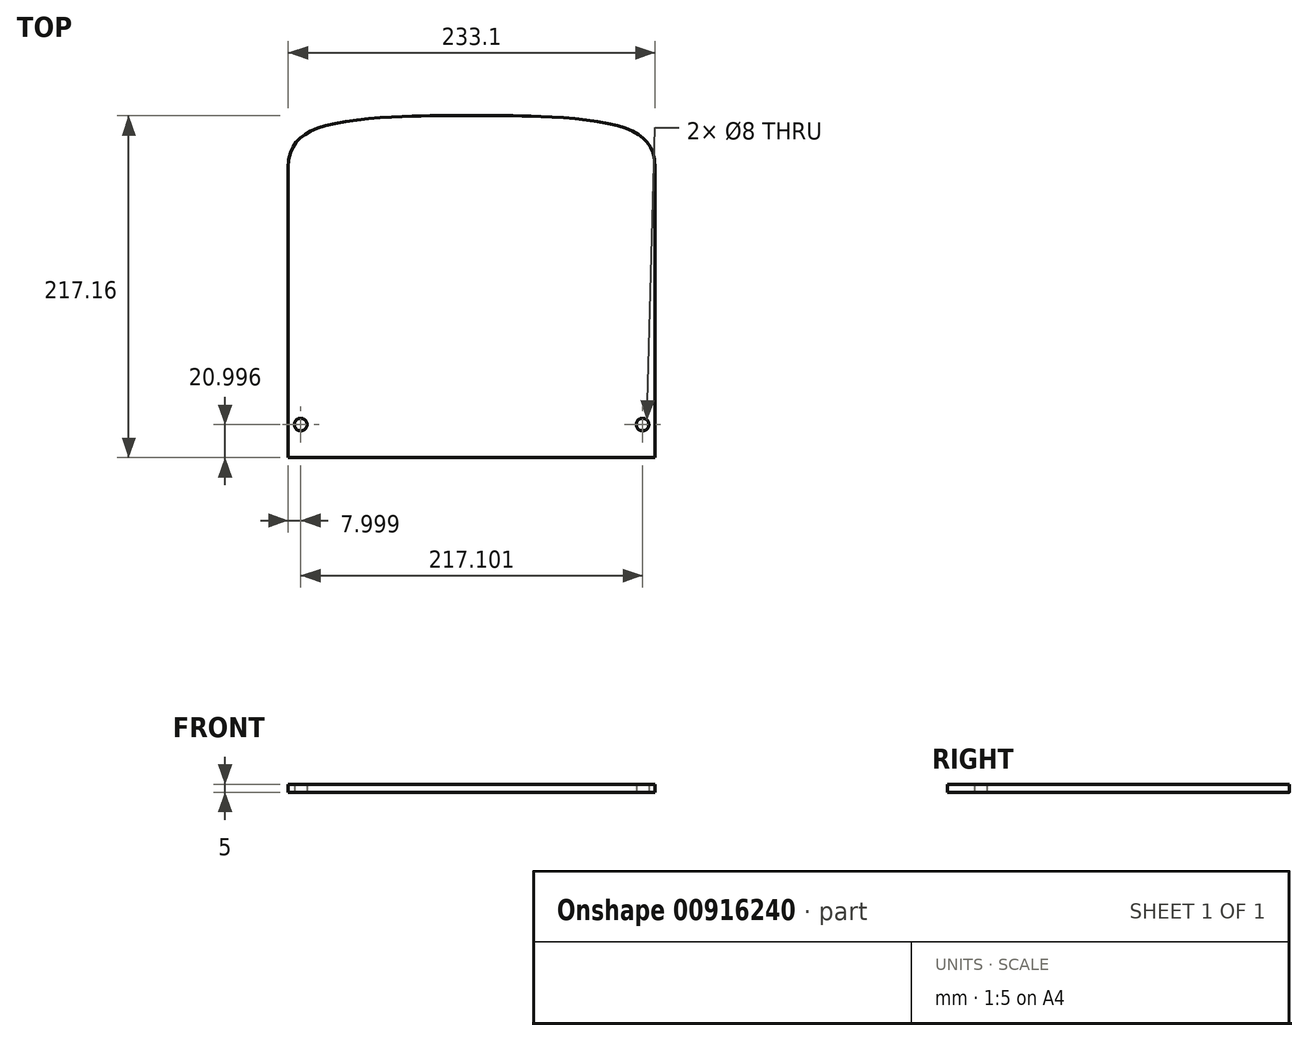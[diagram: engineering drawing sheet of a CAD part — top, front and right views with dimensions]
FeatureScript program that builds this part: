
annotation { "Feature Type Name" : "Feature", "Feature Type Description" : "" }
export const myFeature = defineFeature(function(context is Context, id is Id, definition is map)
    precondition{}
    {
        {
            var Q0;
            Q0=qCreatedBy(makeId("Top.planeOp"),FACE);
            var sketch = newSketch(context, id + "F0", { "sketchPlane" : qUnion([Q0])});
            skLineSegment(sketch, "E0", {"start": v(-119.58, -107.38) * mm, "end": v(-3.03, -107.38) * mm});
            skLineSegment(sketch, "E1", {"start": v(-3.03, -107.38) * mm, "end": v(-3.03, 136.23) * mm, "construction": true});
            skLineSegment(sketch, "E2", {"start": v(-119.58, 76.7) * mm, "end": v(-119.58, -107.38) * mm});
            skPoint(sketch, "E3.orphan", {"position": v(-120.82, -107.38) * mm});
            skFitSpline(sketch, "E4", {"points": [v(-119.58, 76.7) * mm, v(-113.58, 93.96) * mm, v(-95.49, 103.55) * mm, v(-44.74, 109.44) * mm, v(-3.03, 109.78) * mm], "startDerivative": vector(1.3, 133.11) * mm, "endDerivative": vector(192.06, 0.9) * mm});
            skPoint(sketch, "E5.orphan", {"position": v(114.76, -107.38) * mm});
            skLineSegment(sketch, "E6", {"start": v(-111.58, -86.38) * mm, "end": v(-99.99, -93.99) * mm, "construction": true});
            skCircle(sketch, "E7", {"center": v(-111.58, -86.38) * mm, "radius": 4 * mm});
            skPoint(sketch, "E8.MirrorCS.end.orphan", {"position": v(-3.03, -107.38) * mm});
            skPoint(sketch, "E9.MirrorCS.end.orphan", {"position": v(113.52, -107.38) * mm});
            skPoint(sketch, "E9.MirrorCS.start.orphan", {"position": v(113.52, 76.7) * mm});
            skCircle(sketch, "E10.MirrorC", {"center": v(105.52, -86.38) * mm, "radius": 4 * mm});
            skFitSpline(sketch, "E11.MirrorCS", {"points": [v(113.52, 76.7) * mm, v(107.52, 93.96) * mm, v(89.43, 103.55) * mm, v(38.68, 109.44) * mm, v(-3.03, 109.78) * mm], "startDerivative": vector(-1.3, 133.11) * mm, "endDerivative": vector(-192.06, 0.9) * mm});
            skLineSegment(sketch, "E12.MirrorCS", {"start": v(113.52, -107.38) * mm, "end": v(-3.03, -107.38) * mm});
            skLineSegment(sketch, "E13.MirrorCS", {"start": v(113.52, 76.7) * mm, "end": v(113.52, -107.38) * mm});
            skSolve(sketch);
        }
        {
            var Q0;
            Q0 = qSketchRegion(id + "F0", true);
            extrude(context, id + "F1", {"entities" : qUnion([Q0]), "depth" : 5 * mm, "offsetDistance" : 25 * mm});
        }
    });
